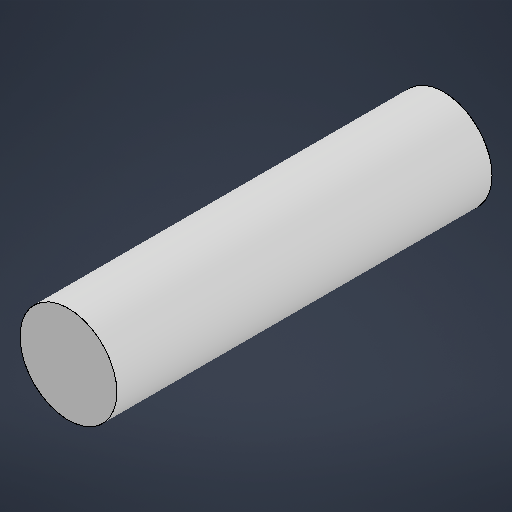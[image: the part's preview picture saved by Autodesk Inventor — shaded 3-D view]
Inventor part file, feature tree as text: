
AUTODESK INVENTOR PART (.ipt)
format: ipt  version: 2025.3 (Build 293356000, 356)  size: 168,960 bytes
history: native  units: mm
features: extrude x1, sketch x1
ambient origin geometry x8: Origin, YZ Plane, XZ Plane, XY Plane, X Axis, Y Axis, Z Axis, Center Point
bodies: Solid1 (feature_tree)
feature tree (2):
  extrude  "Extrusion1"  Depth=11.619mm TaperAngle=0.0deg
  sketch  "Sketch1"  dims[d0=3.0mm d1=11.619mm d2=0.0mm]
